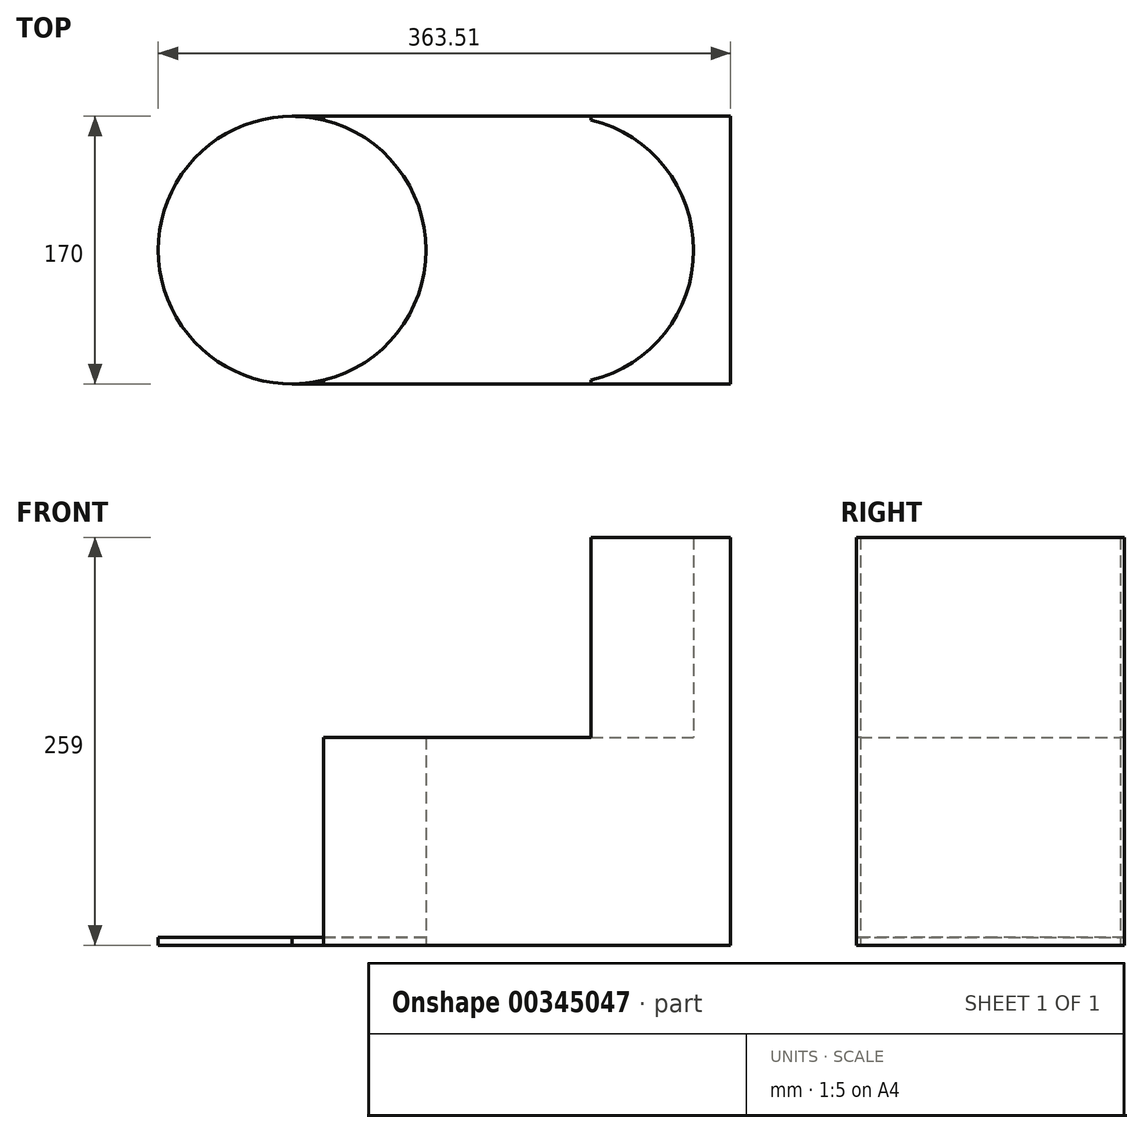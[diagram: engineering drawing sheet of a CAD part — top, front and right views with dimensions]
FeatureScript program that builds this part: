
annotation { "Feature Type Name" : "Feature", "Feature Type Description" : "" }
export const myFeature = defineFeature(function(context is Context, id is Id, definition is map)
    precondition{}
    {
        {
            var Q0;
            Q0=qCreatedBy(makeId("Top.planeOp"),FACE);
            var sketch = newSketch(context, id + "F0", { "sketchPlane" : qUnion([Q0])});
            skCircle(sketch, "E0", {"center": v(0, 0) * mm, "radius": 85 * mm});
            skPoint(sketch, "E1.first.point", {"position": v(85, 0) * mm});
            skPoint(sketch, "E1.second.point", {"position": v(248.51, 0) * mm});
            skLineSegment(sketch, "E2", {"start": v(0, 85) * mm, "end": v(248.51, 85) * mm});
            skLineSegment(sketch, "E3", {"start": v(248.51, 85) * mm, "end": v(278.51, 85) * mm});
            skLineSegment(sketch, "E4", {"start": v(0, -85) * mm, "end": v(248.51, -85) * mm});
            skLineSegment(sketch, "E5", {"start": v(248.51, -85) * mm, "end": v(278.51, -85) * mm});
            skLineSegment(sketch, "E6", {"start": v(278.51, -85) * mm, "end": v(278.51, 85) * mm});
            skCircle(sketch, "E7", {"center": v(170, 0) * mm, "radius": 85 * mm});
            skLineSegment(sketch, "E8", {"start": v(20, 85) * mm, "end": v(20, 82.61) * mm});
            skLineSegment(sketch, "E9", {"start": v(20, -82.61) * mm, "end": v(20, -85) * mm});
            skLineSegment(sketch, "E10", {"start": v(190, 85) * mm, "end": v(190, 82.61) * mm});
            skLineSegment(sketch, "E11", {"start": v(190, -82.61) * mm, "end": v(190, -85) * mm});
            skSolve(sketch);
        }
        {
            var Q0;
            {var subQ0=sQuery(id+"F0.wireOp",EDGE,"E0");var subQ1=makeQuery(id+"F0.imprint","INTERSECT",VERTEX,{"derivedFrom":[subQ0,sQuery(id+"F0.wireOp",EDGE,"E2")]});Q0=makeQuery(id+"F0.imprint","IMPRINT",FACE,{"disambiguationData":[TD([[makeQuery(id+"F0.imprint","IMPRINT",EDGE,{"disambiguationData":[TD([[subQ1,1.0]])],"derivedFrom":subQ0}),1.0]])]});}
            extrude(context, id + "F1", {"entities" : qUnion([Q0]), "depth" : 5 * mm});
        }
        {
            var Q0;
            {var subQ3=sQuery(id+"F0.wireOp",EDGE,"E8");Q0=makeQuery(id+"F0.imprint","IMPRINT",FACE,{"disambiguationData":[TD([[makeQuery(id+"F0.imprint","IMPRINT",EDGE,{"derivedFrom":subQ3}),-1.0]])]});}
            var Q1;
            {var subQ3=sQuery(id+"F0.wireOp",EDGE,"E9");Q1=makeQuery(id+"F0.imprint","IMPRINT",FACE,{"disambiguationData":[TD([[makeQuery(id+"F0.imprint","IMPRINT",EDGE,{"derivedFrom":subQ3}),-1.0]])]});}
            extrude(context, id + "F2", {"entities" : qUnion([Q0, Q1]), "depth" : 5 * mm});
        }
        {
            var Q0;
            {var subQ0=sQuery(id+"F0.wireOp",EDGE,"E9");Q0=makeQuery(id+"F0.imprint","IMPRINT",FACE,{"disambiguationData":[TD([[makeQuery(id+"F0.imprint","IMPRINT",EDGE,{"derivedFrom":subQ0}),1.0]])]});}
            var Q1;
            {var subQ0=sQuery(id+"F0.wireOp",EDGE,"E8");Q1=makeQuery(id+"F0.imprint","IMPRINT",FACE,{"disambiguationData":[TD([[makeQuery(id+"F0.imprint","IMPRINT",EDGE,{"derivedFrom":subQ0}),1.0]])]});}
            var Q2;
            {var subQ0=sQuery(id+"F0.wireOp",EDGE,"E7");var subQ1=makeQuery(id+"F0.imprint","INTERSECT",VERTEX,{"derivedFrom":[sQuery(id+"F0.wireOp",EDGE,"E2"),subQ0]});Q2=makeQuery(id+"F0.imprint","IMPRINT",FACE,{"disambiguationData":[TD([[makeQuery(id+"F0.imprint","IMPRINT",EDGE,{"disambiguationData":[TD([[subQ1,-1.0]])],"derivedFrom":subQ0}),1.0]])]});}
            extrude(context, id + "F3", {"entities" : qUnion([Q0, Q1, Q2]), "depth" : 132 * mm});
        }
        {
            var Q0;
            {var subQ0=sQuery(id+"F0.wireOp",EDGE,"E10");Q0=makeQuery(id+"F0.imprint","IMPRINT",FACE,{"disambiguationData":[TD([[makeQuery(id+"F0.imprint","IMPRINT",EDGE,{"derivedFrom":subQ0}),-1.0]])]});}
            var Q1;
            {var subQ0=sQuery(id+"F0.wireOp",EDGE,"E11");Q1=makeQuery(id+"F0.imprint","IMPRINT",FACE,{"disambiguationData":[TD([[makeQuery(id+"F0.imprint","IMPRINT",EDGE,{"derivedFrom":subQ0}),-1.0]])]});}
            extrude(context, id + "F4", {"entities" : qUnion([Q0, Q1]), "operationType" : NewBodyOperationType.ADD, "depth" : 132 * mm});
        }
        {
            var Q0;
            {var subQ1=sQuery(id+"F0.wireOp",EDGE,"E3");Q0=makeQuery(id+"F0.imprint","IMPRINT",FACE,{"disambiguationData":[TD([[makeQuery(id+"F0.imprint","IMPRINT",EDGE,{"derivedFrom":subQ1}),-1.0]])]});}
            extrude(context, id + "F5", {"entities" : qUnion([Q0]), "operationType" : NewBodyOperationType.ADD, "depth" : 259 * mm});
        }
    });
